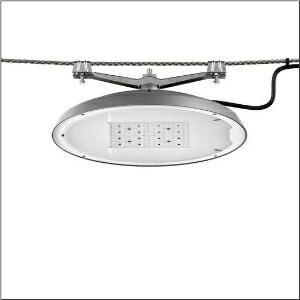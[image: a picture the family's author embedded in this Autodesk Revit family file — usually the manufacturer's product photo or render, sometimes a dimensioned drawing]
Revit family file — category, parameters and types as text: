
# Revit family: dl_r__50_iq_mini___st1_0s_5xa248w41f08le_08ea
name_source: partatom
category: Lighting Fixtures
units: mm (PartAtom-declared; Revit-internal decimal feet)

## family parameters
Cut with Voids When Loaded = No
Host = Face
Light Source = No
Part Type = Normal
Room Calculation Point = No
Round Connector Dimension = Use Diameter
Shared = No

## types (1)
- --- (1 x LED, 10390 lm, 64.1 W, 4000K)
    Apparent Load = 64 VA
    CIE Flux Codes = 37 72 97 100 100
    Color Rendering = 70
    Color Temperature = 4000K
    Default Elevation = 1800 mm
    Description = DL® 50 iQ mini, catenary luminaire, primary light control with lens, of PMMA, primary optical cover: cover, of toughened safety glass, transparent, light distribution: ST1.0s, light emission: direct distribution, primary light characteristic: symmetric, installation type: suspended mounting, LED, High Power LED, rated luminous flux: 10.390lm, luminous efficacy: 162lm/W, light colour: 740, colour temperature: 4000K, control gear: iQ Street-Remote, control: optimised constant luminous flux control (CLO 2.0), Desk-Remote (wireless, voltage-free reading and setting of iQ features in the workshop via application-optimized NFC function/RFID function), Light-Fading, Smart-Wire, Night-Set, Lumen-Switch, Temp-Guard, Auto-Match, Street-Remote, mains connection: 230..240V, AC, 50/60Hz, start of lifetime: 64W, end of service life: 67W, reduction: 30W, luminaire housing, of diecast aluminium, powder-coated, Siteco® metallic grey (DB 702S), diameter: 500mm, height: 115mm, mounting height: 4..12m, protection rating (complete): IP66, insulation class (complete): insulation class II (safety insulation), certification: CE, ENEC, ENEC+, VDE, impact resistance: IK08, permissible operating ambient temperature for outdoor applications: -25..+40°C, standard-compliant lighting for roads and squares, packaging unit: 1 piece

Light Distribution: ST1.0s
    Height = 124 mm  [stored 0.406824 ft]
    Lamp = 1 x LED
    Lamp Light Flux = 10390 lm
    Lamp Power = 64.1 W
    Lamp count = 1
    Length = 500 mm
    Luminous efficacy = 162 lm/W
    Manufacturer = Siteco
    ModVariant = No
    Model = 5XA248W41F08LE
    Number of Poles = 1
    OnlyDefault = Yes
    Power Factor = 1
    Product Name = DL® 50 iQ mini | ST1.0s
    Product group = catenary luminaire
    ProductGroupID = 6300
    Protection Class = Protection class II
    Protection Degree = IP 66
    RLX_Detail_Level = 1
    RLX_Emergency_Light_Flux = 0 lm
    RLX_Emergency_Type = 0
    RLX_Emergency_Type_DB = No
    RlxData = <blob elided: 127197 chars, md5=9497fa79>
    Socket = socket
    Standby Power = 0 W
    System Light Flux = 10390 lm
    System Power = 64 W
    Type Comments = factory setting: luminous flux: 100 % | dim-lin: 254 | 672 mA
    Type Image = l_1251783.jpg
    URL = http://relux.com
    VarID = @adj_140488
    Voltage = 0 V
    Weight = 0.00 kg
    Width = 0 mm  [stored 0 ft]

note: [stored X ft] marks values corroborated as IEEE doubles in the binary element streams (Revit-internal decimal feet)

## geometry (parser evidence)
native form markers: Blend x4, Sweep x13
no freeform markers — native parametric forms only
